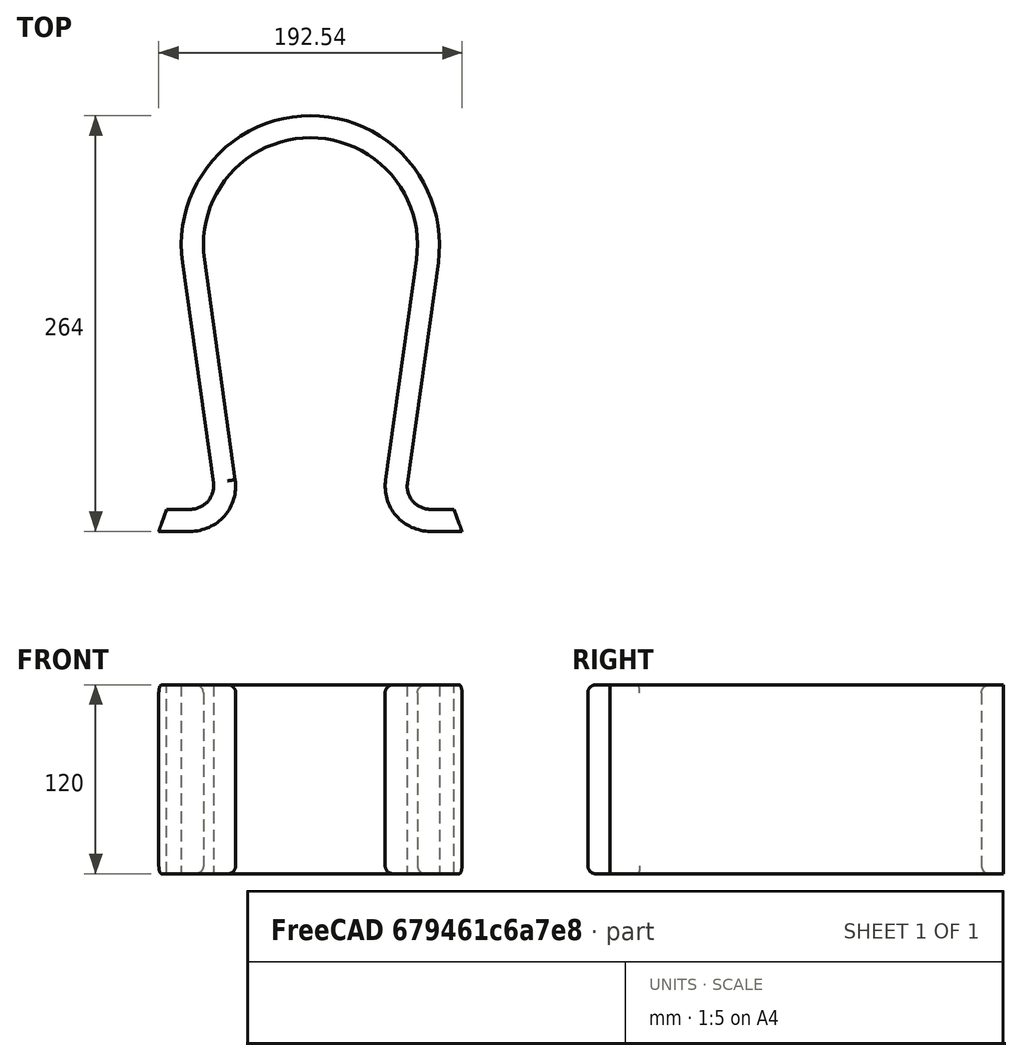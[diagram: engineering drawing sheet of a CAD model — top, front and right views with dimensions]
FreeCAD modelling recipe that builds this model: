
FCSTD DOCUMENT  (FreeCAD 0.22R37898 (Git))
Label: Sin nombre
License: All rights reserved
objects: Sketcher::SketchObject×1, PartDesign::Pad×1, PartDesign::Fillet×1, PartDesign::Body×1
note: 6 computed .brp shape members not serialized (recipe doc carries the construction recipe); baked Part::Feature solids carry a one-line shape summary decoded from their .brp

FEATURE [Sketcher::SketchObject] Sketch
  AttachmentSupport = -> [XY_Plane]
  FullyConstrained = false
  MapMode = 5
  sketch-geometry (31):
    g0: LineSegment StartX=0 StartY=0 StartZ=0 EndX=0 EndY=250 EndZ=0
    g1: LineSegment StartX=-0.00406372 StartY=175.011 StartZ=0 EndX=63.6948 EndY=0 EndZ=0
    g2: LineSegment StartX=0 StartY=0 StartZ=0 EndX=0 EndY=250 EndZ=0
    g3: LineSegment StartX=-74.2734 StartY=164.586 StartZ=0 EndX=74.2734 EndY=164.586 EndZ=0
    g4: LineSegment StartX=-27.2941 StartY=100.01 StartZ=0 EndX=27.2941 EndY=100.01 EndZ=0
    g5: LineSegment StartX=-27.2978 StartY=100.01 StartZ=0 EndX=27.2941 EndY=100.01 EndZ=0
    g6: LineSegment StartX=-63.6948 StartY=0 StartZ=0 EndX=0.0120649 EndY=175.033 EndZ=0
    g7: LineSegment StartX=-74.2734 StartY=164.586 StartZ=0 EndX=-54.6716 EndY=24.7909 EndZ=0
    g8: LineSegment StartX=74.2734 StartY=164.586 StartZ=0 EndX=54.6716 EndY=24.7909 EndZ=0
    g9: ArcOfCircle CenterX=1.3e-15 CenterY=175 CenterZ=0 NormalX=0 NormalY=0 NormalZ=1 AngleXU=0 Radius=75 StartAngle=6.14388 EndAngle=9.56409
    g10: ArcOfCircle CenterX=-76.3127 CenterY=21.841 CenterZ=0 NormalX=0 NormalY=0 NormalZ=1 AngleXU=0 Radius=21.841 StartAngle=4.71239 EndAngle=6.4225
    g11: ArcOfCircle CenterX=76.229 CenterY=21.7683 CenterZ=0 NormalX=0 NormalY=0 NormalZ=1 AngleXU=0 Radius=21.7683 StartAngle=3.00228 EndAngle=4.71239
    g12: LineSegment StartX=-98.1537 StartY=21.841 StartZ=0 EndX=97.9972 EndY=21.841 EndZ=0
    g13: LineSegment StartX=76.229 StartY=21.7683 StartZ=0 EndX=76.229 EndY=1.78e-14 EndZ=0
    g14: LineSegment StartX=-76.3127 StartY=21.841 StartZ=0 EndX=-76.3127 EndY=0 EndZ=0
    g15: ArcOfCircle CenterX=8.5e-15 CenterY=175 CenterZ=0 NormalX=0 NormalY=0 NormalZ=1 AngleXU=0 Radius=82 StartAngle=6.14388 EndAngle=9.56409
    g16: ArcOfCircle CenterX=6.46e-14 CenterY=175 CenterZ=0 NormalX=0 NormalY=0 NormalZ=1 AngleXU=0 Radius=68 StartAngle=6.14388 EndAngle=9.56409
    g17: LineSegment StartX=-76.3114 StartY=-6.98913 StartZ=0 EndX=-96.3114 EndY=-6.98913 EndZ=0
    g18: LineSegment StartX=-76.3127 StartY=7 StartZ=0 EndX=-91.3127 EndY=7 EndZ=0
    g19: LineSegment StartX=76.229 StartY=7 StartZ=0 EndX=91.229 EndY=7 EndZ=0
    g20: LineSegment StartX=76.229 StartY=-7 StartZ=0 EndX=96.229 EndY=-7 EndZ=0
    g21: ArcOfCircle CenterX=-76.3127 CenterY=21.841 CenterZ=0 NormalX=0 NormalY=0 NormalZ=1 AngleXU=0 Radius=14.841 StartAngle=4.71239 EndAngle=6.41685
    g22: ArcOfCircle CenterX=-76.3127 CenterY=21.841 CenterZ=0 NormalX=0 NormalY=0 NormalZ=1 AngleXU=0 Radius=28.8301 StartAngle=4.71243 EndAngle=6.41959
    g23: ArcOfCircle CenterX=76.229 CenterY=21.7683 CenterZ=0 NormalX=0 NormalY=0 NormalZ=1 AngleXU=0 Radius=14.7683 StartAngle=3.00229 EndAngle=4.71239
    g24: ArcOfCircle CenterX=76.229 CenterY=21.7683 CenterZ=0 NormalX=0 NormalY=0 NormalZ=1 AngleXU=0 Radius=28.7683 StartAngle=3.00229 EndAngle=4.71239
    g25: LineSegment StartX=-91.3127 StartY=7 StartZ=0 EndX=-96.3114 EndY=-6.98913 EndZ=0
    g26: LineSegment StartX=91.229 StartY=7 StartZ=0 EndX=96.229 EndY=-7 EndZ=0
    g27: LineSegment StartX=-61.604 StartY=23.8189 StartZ=0 EndX=-81.2056 EndY=163.613 EndZ=0
    g28: LineSegment StartX=-67.3412 StartY=165.558 StartZ=0 EndX=-47.7503 EndY=25.7615 EndZ=0
    g29: LineSegment StartX=81.2056 StartY=163.613 StartZ=0 EndX=61.6038 EndY=23.8189 EndZ=0
    g30: LineSegment StartX=67.3412 StartY=165.558 StartZ=0 EndX=47.7394 EndY=25.763 EndZ=0
  constraints (63):
    c: Distance(g0) = 250
    c: Coincident(g0,g-1)
    c: PointOnObject(g0,g-2)
    c: Angle(g0,g1) = 0.349066
    c: PointOnObject(g1,g-1)
    c: Distance(g2) = 250
    c: Horizontal(g4)
    c: Horizontal(g5)
    c: PointOnObject(g4,g1)
    c: Angle(g6,g0) = 0.349066
    c: PointOnObject(g6,g-1)
    c: PointOnObject(g4,g6)
    c: PointOnObject(g5,g4)
    c: PointOnObject(g5,g1)
    c: Coincident(g7,g3)
    c: Coincident(g8,g3)
    c: Coincident(g9,g7) = -1.5708
    c: Block(g7)
    c: Block(g8)
    c: Tangent(g10,g-1)
    c: Horizontal(g12)
    c: PointOnObject(g10,g12)
    c: Coincident(g13,g11)
    c: Vertical(g13)
    c: Coincident(g14,g10)
    c: Vertical(g14)
    c: Tangent(g10,g7) = 1.5708
    c: Coincident(g10,g14)
    c: Tangent(g11,g8) = -1.5708
    c: Coincident(g11,g13)
    c: Distance(g17) = 20
    c: Horizontal(g17)
    c: Distance(g18) = 15
    c: Horizontal(g18)
    c: Distance(g19) = 15
    c: Horizontal(g19)
    c: Distance(g20) = 20
    c: Horizontal(g20)
    c: Coincident(g21,g18)
    c: Coincident(g22,g21)
    c: Coincident(g22,g17)
    c: Coincident(g23,g11)
    c: Coincident(g23,g19)
    c: Coincident(g24,g11)
    c: Coincident(g24,g20)
    c: Block(g21)
    c: Block(g22)
    c: Block(g24)
    c: Block(g23)
    c: Coincident(g25,g18)
    c: Coincident(g25,g17)
    c: Coincident(g26,g19)
    c: Coincident(g26,g20)
    c: Coincident(g27,g21)
    c: Coincident(g27,g15)
    c: Coincident(g28,g16)
    c: Coincident(g28,g22)
    c: Coincident(g29,g15)
    c: Coincident(g29,g23)
    c: Block(g16)
    c: Block(g15)
    c: Coincident(g30,g16)
    c: Coincident(g30,g24)
FEATURE [PartDesign::Pad] Pad
  Direction = (0,0,1)
  Length = 120
  Length2 = 10
  Profile = -> Sketch
  ReferenceAxis = -> Sketch [N_Axis]
  Refine = true
  Suppressed = false
  Type = 0
FEATURE [PartDesign::Fillet] Fillet
  Base = -> Pad [Edge33,Edge36,Edge37,Edge34,Edge30,Edge27,Edge28,Edge24,Edge21,Edge18,Edge19,Edge22,Edge25,Edge31]
  BaseFeature = -> Pad
  Radius = 5
  Refine = true
  SupportTransform = false
  Suppressed = false
  UseAllEdges = false
FEATURE [PartDesign::Body] Body  label="headset stand"
  AllowCompound = false
  Group = -> [Sketch,Pad,Fillet]
  Origin = -> Origin
  Tip = -> Fillet
